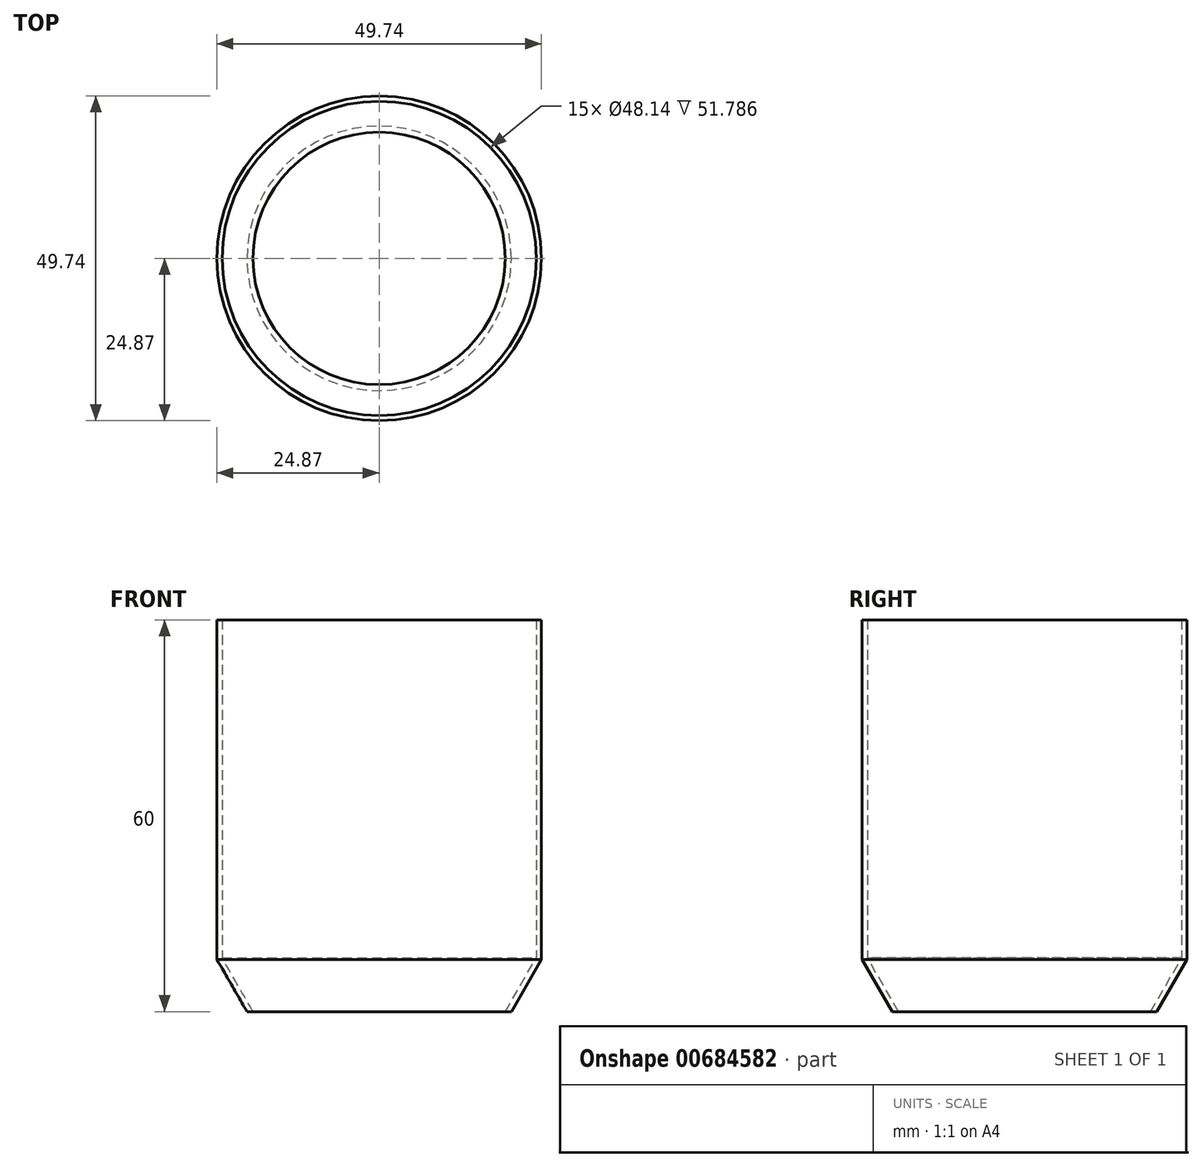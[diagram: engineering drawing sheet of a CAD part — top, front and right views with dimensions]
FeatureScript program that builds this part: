
annotation { "Feature Type Name" : "Feature", "Feature Type Description" : "" }
export const myFeature = defineFeature(function(context is Context, id is Id, definition is map)
    precondition{}
    {
        {
            var Q0;
            Q0=qCreatedBy(makeId("Front.planeOp"),FACE);
            var sketch = newSketch(context, id + "F0", { "sketchPlane" : qUnion([Q0])});
            skLineSegment(sketch, "E0", {"start": v(-20.25, 0) * mm, "end": v(-24.87, 8) * mm});
            skLineSegment(sketch, "E1", {"start": v(-24.87, 8) * mm, "end": v(-24.87, 60) * mm});
            skLineSegment(sketch, "E2.0", {"start": v(-24.07, 8.21) * mm, "end": v(-24.07, 60) * mm});
            skLineSegment(sketch, "E2.1", {"start": v(-19.33, 0) * mm, "end": v(-24.07, 8.21) * mm});
            skLineSegment(sketch, "E3", {"start": v(-20.25, 0) * mm, "end": v(-19.33, 0) * mm});
            skLineSegment(sketch, "E4", {"start": v(-24.87, 60) * mm, "end": v(-24.07, 60) * mm});
            skLineSegment(sketch, "E5", {"start": v(0, 8.42) * mm, "end": v(0, 27.24) * mm, "construction": true});
            skSolve(sketch);
        }
        {
            var Q0;
            Q0 = qSketchRegion(id + "F0", true);
            var Q1;
            Q1=sQuery(id+"F0.wireOp",EDGE,"E5");
            revolve(context, id + "F1", {"entities" : qUnion([Q0]), "axis" : qUnion([Q1]), "revolveType" : RevolveType.FULL});
        }
    });
